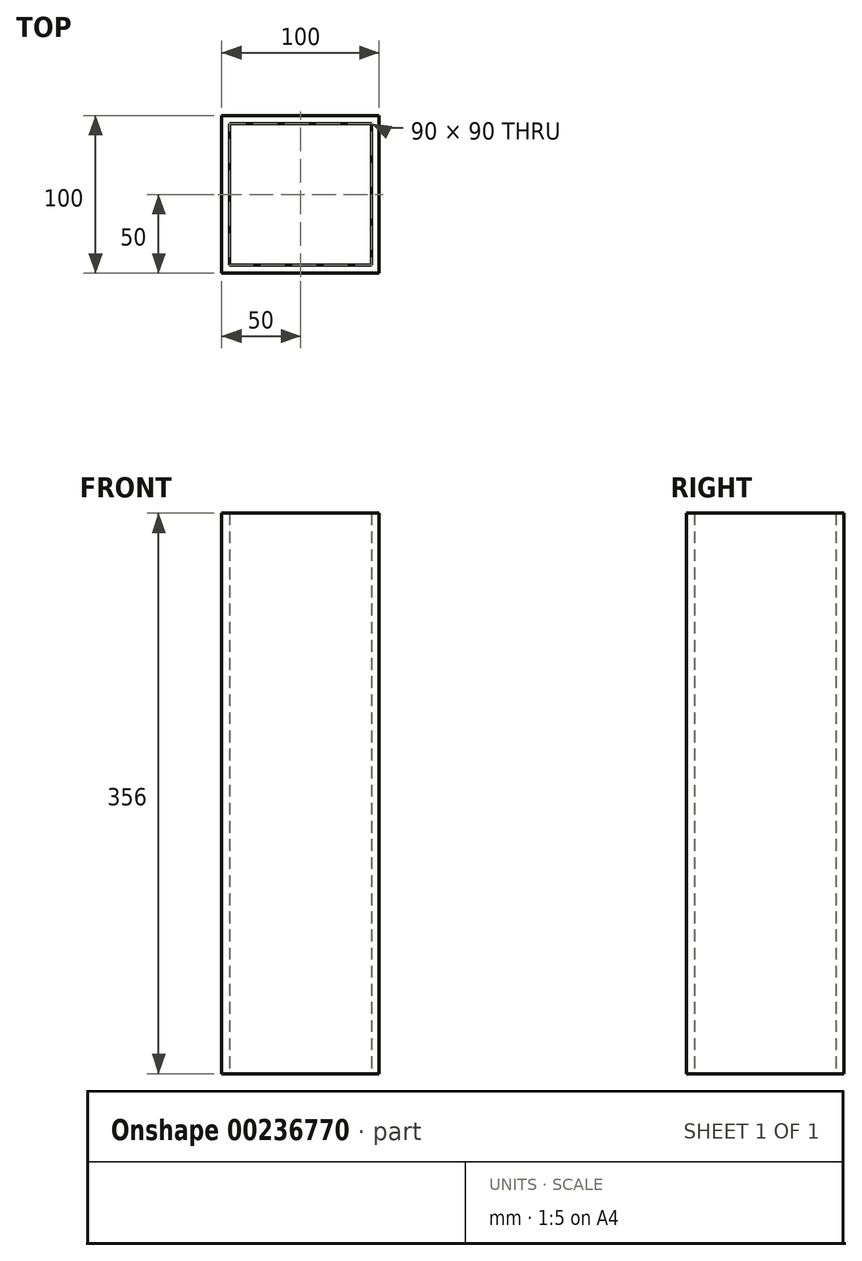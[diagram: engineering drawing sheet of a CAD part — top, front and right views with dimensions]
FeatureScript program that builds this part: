
annotation { "Feature Type Name" : "Feature", "Feature Type Description" : "" }
export const myFeature = defineFeature(function(context is Context, id is Id, definition is map)
    precondition{}
    {
        {
            var Q0;
            Q0=qCreatedBy(makeId("Top.planeOp"),FACE);
            var sketch = newSketch(context, id + "F0", { "sketchPlane" : qUnion([Q0])});
            skLineSegment(sketch, "E0.bottom", {"start": v(50, 50) * mm, "end": v(-50, 50) * mm});
            skLineSegment(sketch, "E0.top", {"start": v(50, -50) * mm, "end": v(-50, -50) * mm});
            skLineSegment(sketch, "E0.left", {"start": v(50, 50) * mm, "end": v(50, -50) * mm});
            skLineSegment(sketch, "E0.right", {"start": v(-50, 50) * mm, "end": v(-50, -50) * mm});
            skPoint(sketch, "E0.middle", {"position": v(0, 0) * mm});
            skLineSegment(sketch, "E1.bottom", {"start": v(45, 45) * mm, "end": v(-45, 45) * mm});
            skLineSegment(sketch, "E1.top", {"start": v(45, -45) * mm, "end": v(-45, -45) * mm});
            skLineSegment(sketch, "E1.left", {"start": v(45, 45) * mm, "end": v(45, -45) * mm});
            skLineSegment(sketch, "E1.right", {"start": v(-45, 45) * mm, "end": v(-45, -45) * mm});
            skSolve(sketch);
        }
        {
            var Q0;
            Q0 = qSketchRegion(id + "F0", true);
            extrude(context, id + "F1", {"entities" : qUnion([Q0]), "depth" : 356 * mm, "offsetDistance" : 25 * mm});
        }
    });
